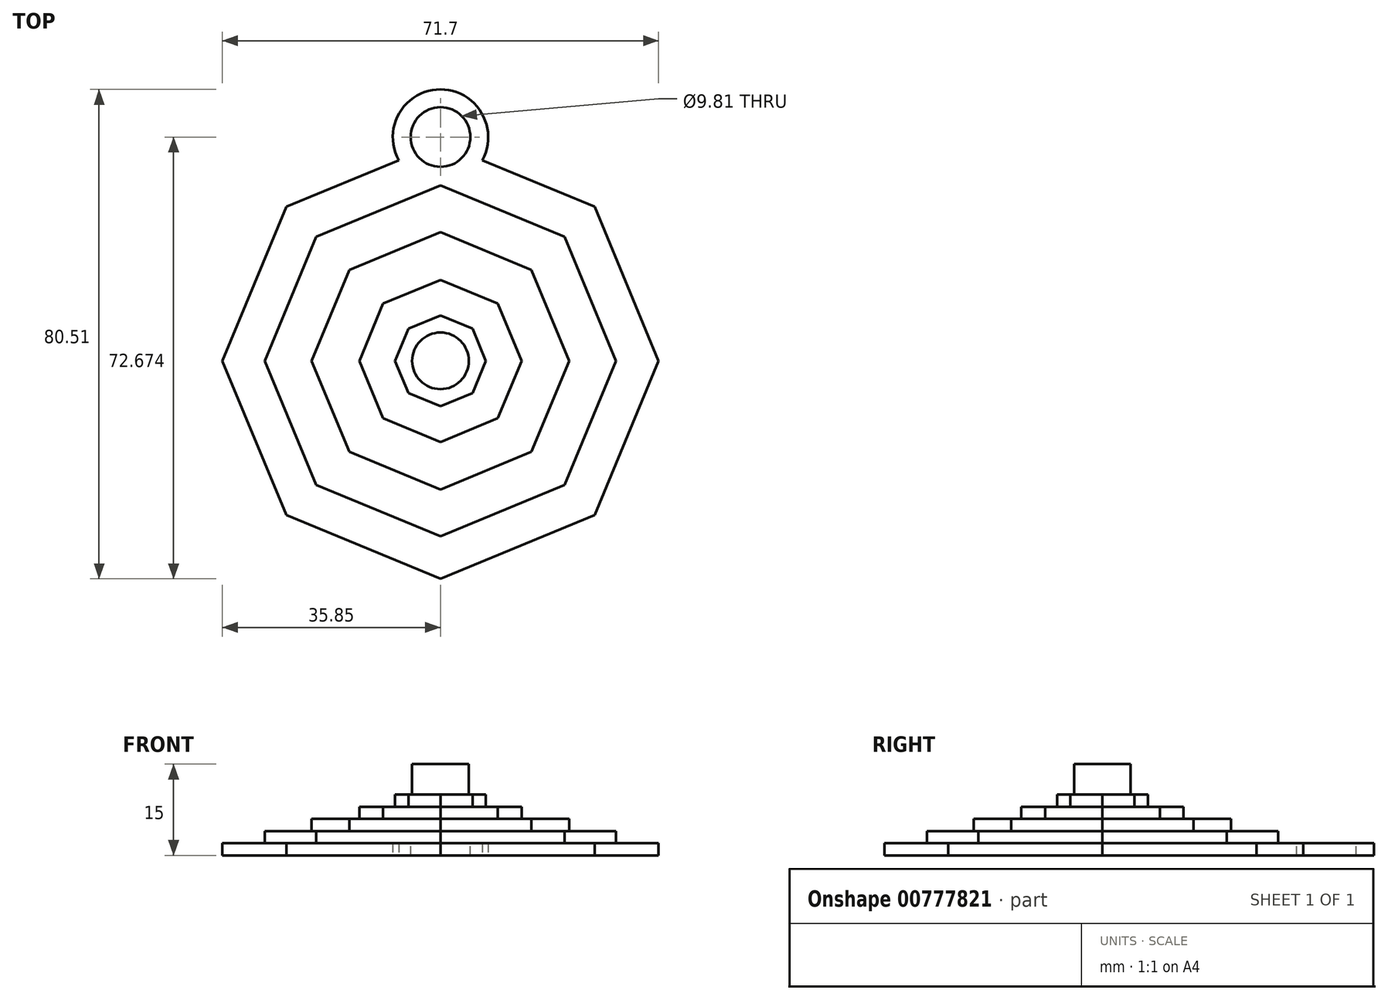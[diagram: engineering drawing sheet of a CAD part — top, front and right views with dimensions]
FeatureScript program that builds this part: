
annotation { "Feature Type Name" : "Feature", "Feature Type Description" : "" }
export const myFeature = defineFeature(function(context is Context, id is Id, definition is map)
    precondition{}
    {
        {
            var Q0;
            Q0=qCreatedBy(makeId("Top.planeOp"),FACE);
            var sketch = newSketch(context, id + "F0", { "sketchPlane" : qUnion([Q0])});
            skCircle(sketch, "E0.cCircle", {"center": v(0, 0) * mm, "radius": 35.85 * mm, "construction": true});
            skLineSegment(sketch, "E0.0", {"start": v(0, 35.85) * mm, "end": v(25.35, 25.35) * mm});
            skLineSegment(sketch, "E0.1", {"start": v(25.35, 25.35) * mm, "end": v(35.85, 0) * mm});
            skLineSegment(sketch, "E0.2", {"start": v(35.85, 0) * mm, "end": v(25.35, -25.35) * mm});
            skLineSegment(sketch, "E0.3", {"start": v(25.35, -25.35) * mm, "end": v(0, -35.85) * mm});
            skLineSegment(sketch, "E0.4", {"start": v(0, -35.85) * mm, "end": v(-25.35, -25.35) * mm});
            skLineSegment(sketch, "E0.5", {"start": v(-25.35, -25.35) * mm, "end": v(-35.85, 0) * mm});
            skLineSegment(sketch, "E0.6", {"start": v(-35.85, 0) * mm, "end": v(-25.35, 25.35) * mm});
            skLineSegment(sketch, "E0.7", {"start": v(-25.35, 25.35) * mm, "end": v(0, 35.85) * mm});
            skSolve(sketch);
        }
        {
            var Q0;
            Q0=makeQuery(id+"F0.imprint","IMPRINT",FACE,{"disambiguationData":[TD([[makeQuery(id+"F0.imprint","IMPRINT",EDGE,{"derivedFrom":sQuery(id+"F0.wireOp",EDGE,"E0.0")}),-1.0]])]});
            extrude(context, id + "F1", {"entities" : qUnion([Q0]), "depth" : 2 * mm, "offsetDistance" : 25.4 * mm});
        }
        {
            var Q0;
            Q0=makeQuery(id+"F1.opExtrude","CAP_FACE",FACE,{"disambiguationData":[OSD([sQuery(id+"F0.wireOp",EDGE,"E0.0"),sQuery(id+"F0.wireOp",EDGE,"E0.1"),sQuery(id+"F0.wireOp",EDGE,"E0.2"),sQuery(id+"F0.wireOp",EDGE,"E0.3"),sQuery(id+"F0.wireOp",EDGE,"E0.4"),sQuery(id+"F0.wireOp",EDGE,"E0.5"),sQuery(id+"F0.wireOp",EDGE,"E0.6"),sQuery(id+"F0.wireOp",EDGE,"E0.7")])],"isStart":false});
            var sketch = newSketch(context, id + "F2", { "sketchPlane" : qUnion([Q0])});
            skCircle(sketch, "E1.cCircle", {"center": v(0, 0) * mm, "radius": 28.87 * mm, "construction": true});
            skLineSegment(sketch, "E1.0", {"start": v(0, 28.87) * mm, "end": v(20.42, 20.42) * mm});
            skLineSegment(sketch, "E1.1", {"start": v(20.42, 20.42) * mm, "end": v(28.87, 0) * mm});
            skLineSegment(sketch, "E1.2", {"start": v(28.87, 0) * mm, "end": v(20.42, -20.42) * mm});
            skLineSegment(sketch, "E1.3", {"start": v(20.42, -20.42) * mm, "end": v(0, -28.87) * mm});
            skLineSegment(sketch, "E1.4", {"start": v(0, -28.87) * mm, "end": v(-20.42, -20.42) * mm});
            skLineSegment(sketch, "E1.5", {"start": v(-20.42, -20.42) * mm, "end": v(-28.87, 0) * mm});
            skLineSegment(sketch, "E1.6", {"start": v(-28.87, 0) * mm, "end": v(-20.42, 20.42) * mm});
            skLineSegment(sketch, "E1.7", {"start": v(-20.42, 20.42) * mm, "end": v(0, 28.87) * mm});
            skSolve(sketch);
        }
        {
            var Q0;
            Q0 = qSketchRegion(id + "F2", true);
            extrude(context, id + "F3", {"entities" : qUnion([Q0]), "operationType" : NewBodyOperationType.ADD, "depth" : 2 * mm, "offsetDistance" : 25.4 * mm});
        }
        {
            var Q0;
            Q0=makeQuery(id+"F3.opExtrude","CAP_FACE",FACE,{"disambiguationData":[OSD([sQuery(id+"F2.wireOp",EDGE,"E1.0"),sQuery(id+"F2.wireOp",EDGE,"E1.1"),sQuery(id+"F2.wireOp",EDGE,"E1.2"),sQuery(id+"F2.wireOp",EDGE,"E1.3"),sQuery(id+"F2.wireOp",EDGE,"E1.4"),sQuery(id+"F2.wireOp",EDGE,"E1.5"),sQuery(id+"F2.wireOp",EDGE,"E1.6"),sQuery(id+"F2.wireOp",EDGE,"E1.7")])],"isStart":false});
            var sketch = newSketch(context, id + "F4", { "sketchPlane" : qUnion([Q0])});
            skCircle(sketch, "E2.cCircle", {"center": v(0, 0) * mm, "radius": 21.16 * mm, "construction": true});
            skLineSegment(sketch, "E2.0", {"start": v(0, 21.16) * mm, "end": v(14.97, 14.97) * mm});
            skLineSegment(sketch, "E2.1", {"start": v(14.97, 14.97) * mm, "end": v(21.16, 0) * mm});
            skLineSegment(sketch, "E2.2", {"start": v(21.16, 0) * mm, "end": v(14.97, -14.97) * mm});
            skLineSegment(sketch, "E2.3", {"start": v(14.97, -14.97) * mm, "end": v(0, -21.16) * mm});
            skLineSegment(sketch, "E2.4", {"start": v(0, -21.16) * mm, "end": v(-14.97, -14.97) * mm});
            skLineSegment(sketch, "E2.5", {"start": v(-14.97, -14.97) * mm, "end": v(-21.16, 0) * mm});
            skLineSegment(sketch, "E2.6", {"start": v(-21.16, 0) * mm, "end": v(-14.97, 14.97) * mm});
            skLineSegment(sketch, "E2.7", {"start": v(-14.97, 14.97) * mm, "end": v(0, 21.16) * mm});
            skSolve(sketch);
        }
        {
            var Q0;
            Q0=makeQuery(id+"F4.imprint","IMPRINT",FACE,{"disambiguationData":[TD([[makeQuery(id+"F4.imprint","IMPRINT",EDGE,{"derivedFrom":sQuery(id+"F4.wireOp",EDGE,"E2.0")}),-1.0]])]});
            extrude(context, id + "F5", {"entities" : qUnion([Q0]), "operationType" : NewBodyOperationType.ADD, "depth" : 2 * mm, "offsetDistance" : 25.4 * mm});
        }
        {
            var Q0;
            Q0=makeQuery(id+"F5.opExtrude","CAP_FACE",FACE,{"disambiguationData":[OSD([sQuery(id+"F4.wireOp",EDGE,"E2.0"),sQuery(id+"F4.wireOp",EDGE,"E2.1"),sQuery(id+"F4.wireOp",EDGE,"E2.2"),sQuery(id+"F4.wireOp",EDGE,"E2.3"),sQuery(id+"F4.wireOp",EDGE,"E2.4"),sQuery(id+"F4.wireOp",EDGE,"E2.5"),sQuery(id+"F4.wireOp",EDGE,"E2.6"),sQuery(id+"F4.wireOp",EDGE,"E2.7")])],"isStart":false});
            var sketch = newSketch(context, id + "F6", { "sketchPlane" : qUnion([Q0])});
            skCircle(sketch, "E3.cCircle", {"center": v(0, 0) * mm, "radius": 13.34 * mm, "construction": true});
            skLineSegment(sketch, "E3.0", {"start": v(0, 13.34) * mm, "end": v(9.43, 9.43) * mm});
            skLineSegment(sketch, "E3.1", {"start": v(9.43, 9.43) * mm, "end": v(13.34, 0) * mm});
            skLineSegment(sketch, "E3.2", {"start": v(13.34, 0) * mm, "end": v(9.43, -9.43) * mm});
            skLineSegment(sketch, "E3.3", {"start": v(9.43, -9.43) * mm, "end": v(0, -13.34) * mm});
            skLineSegment(sketch, "E3.4", {"start": v(0, -13.34) * mm, "end": v(-9.43, -9.43) * mm});
            skLineSegment(sketch, "E3.5", {"start": v(-9.43, -9.43) * mm, "end": v(-13.34, 0) * mm});
            skLineSegment(sketch, "E3.6", {"start": v(-13.34, 0) * mm, "end": v(-9.43, 9.43) * mm});
            skLineSegment(sketch, "E3.7", {"start": v(-9.43, 9.43) * mm, "end": v(0, 13.34) * mm});
            skSolve(sketch);
        }
        {
            var Q0;
            Q0=makeQuery(id+"F6.imprint","IMPRINT",FACE,{"disambiguationData":[TD([[makeQuery(id+"F6.imprint","IMPRINT",EDGE,{"derivedFrom":sQuery(id+"F6.wireOp",EDGE,"E3.0")}),-1.0]])]});
            extrude(context, id + "F7", {"entities" : qUnion([Q0]), "operationType" : NewBodyOperationType.ADD, "depth" : 2 * mm, "offsetDistance" : 25.4 * mm});
        }
        {
            var Q0;
            Q0=makeQuery(id+"F7.opExtrude","CAP_FACE",FACE,{"disambiguationData":[OSD([sQuery(id+"F6.wireOp",EDGE,"E3.0"),sQuery(id+"F6.wireOp",EDGE,"E3.1"),sQuery(id+"F6.wireOp",EDGE,"E3.2"),sQuery(id+"F6.wireOp",EDGE,"E3.3"),sQuery(id+"F6.wireOp",EDGE,"E3.4"),sQuery(id+"F6.wireOp",EDGE,"E3.5"),sQuery(id+"F6.wireOp",EDGE,"E3.6"),sQuery(id+"F6.wireOp",EDGE,"E3.7")])],"isStart":false});
            var sketch = newSketch(context, id + "F8", { "sketchPlane" : qUnion([Q0])});
            skCircle(sketch, "E4.cCircle", {"center": v(0, 0) * mm, "radius": 7.46 * mm, "construction": true});
            skLineSegment(sketch, "E4.0", {"start": v(0, 7.46) * mm, "end": v(5.28, 5.28) * mm});
            skLineSegment(sketch, "E4.1", {"start": v(5.28, 5.28) * mm, "end": v(7.46, 0) * mm});
            skLineSegment(sketch, "E4.2", {"start": v(7.46, 0) * mm, "end": v(5.28, -5.28) * mm});
            skLineSegment(sketch, "E4.3", {"start": v(5.28, -5.28) * mm, "end": v(0, -7.46) * mm});
            skLineSegment(sketch, "E4.4", {"start": v(0, -7.46) * mm, "end": v(-5.28, -5.28) * mm});
            skLineSegment(sketch, "E4.5", {"start": v(-5.28, -5.28) * mm, "end": v(-7.46, 0) * mm});
            skLineSegment(sketch, "E4.6", {"start": v(-7.46, 0) * mm, "end": v(-5.28, 5.28) * mm});
            skLineSegment(sketch, "E4.7", {"start": v(-5.28, 5.28) * mm, "end": v(0, 7.46) * mm});
            skSolve(sketch);
        }
        {
            var Q0;
            Q0=makeQuery(id+"F8.imprint","IMPRINT",FACE,{"disambiguationData":[TD([[makeQuery(id+"F8.imprint","IMPRINT",EDGE,{"derivedFrom":sQuery(id+"F8.wireOp",EDGE,"E4.0")}),-1.0]])]});
            extrude(context, id + "F9", {"entities" : qUnion([Q0]), "operationType" : NewBodyOperationType.ADD, "depth" : 2 * mm, "offsetDistance" : 25.4 * mm});
        }
        {
            var Q0;
            Q0=qCreatedBy(makeId("Top.planeOp"),FACE);
            var sketch = newSketch(context, id + "F10", { "sketchPlane" : qUnion([Q0])});
            skCircle(sketch, "E5", {"center": v(0, 36.82) * mm, "radius": 7.84 * mm});
            skSolve(sketch);
        }
        {
            var Q0;
            Q0=makeQuery(id+"F10.imprint","IMPRINT",FACE,{"disambiguationData":[TD([[makeQuery(id+"F10.imprint","IMPRINT",EDGE,{"derivedFrom":sQuery(id+"F10.wireOp",EDGE,"E5")}),1.0]])]});
            extrude(context, id + "F11", {"entities" : qUnion([Q0]), "operationType" : NewBodyOperationType.ADD, "depth" : 2 * mm, "offsetDistance" : 25.4 * mm});
        }
        {
            var Q0;
            Q0=makeQuery(id+"F11.boolean.opBoolean","MERGE",FACE,{"derivedFrom":[makeQuery(id+"F1.opExtrude","CAP_FACE",FACE,{"disambiguationData":[OSD([sQuery(id+"F0.wireOp",EDGE,"E0.0"),sQuery(id+"F0.wireOp",EDGE,"E0.1"),sQuery(id+"F0.wireOp",EDGE,"E0.2"),sQuery(id+"F0.wireOp",EDGE,"E0.3"),sQuery(id+"F0.wireOp",EDGE,"E0.4"),sQuery(id+"F0.wireOp",EDGE,"E0.5"),sQuery(id+"F0.wireOp",EDGE,"E0.6"),sQuery(id+"F0.wireOp",EDGE,"E0.7")])],"isStart":false}),makeQuery(id+"F11.opExtrude","CAP_FACE",FACE,{"disambiguationData":[OSD([sQuery(id+"F10.wireOp",EDGE,"E5")])],"isStart":false})]});
            var sketch = newSketch(context, id + "F12", { "sketchPlane" : qUnion([Q0])});
            skCircle(sketch, "E6", {"center": v(0, 36.82) * mm, "radius": 4.9 * mm});
            skSolve(sketch);
        }
        {
            var Q0;
            Q0=makeQuery(id+"F12.imprint","IMPRINT",FACE,{"disambiguationData":[TD([[makeQuery(id+"F12.imprint","IMPRINT",EDGE,{"derivedFrom":sQuery(id+"F12.wireOp",EDGE,"E6")}),1.0]])]});
            extrude(context, id + "F13", {"entities" : qUnion([Q0]), "operationType" : NewBodyOperationType.REMOVE, "oppositeDirection" : true, "depth" : 25.4 * mm, "offsetDistance" : 25.4 * mm});
        }
        {
            var Q0;
            Q0=makeQuery(id+"F9.opExtrude","CAP_FACE",FACE,{"disambiguationData":[OSD([sQuery(id+"F8.wireOp",EDGE,"E4.0"),sQuery(id+"F8.wireOp",EDGE,"E4.1"),sQuery(id+"F8.wireOp",EDGE,"E4.2"),sQuery(id+"F8.wireOp",EDGE,"E4.3"),sQuery(id+"F8.wireOp",EDGE,"E4.4"),sQuery(id+"F8.wireOp",EDGE,"E4.5"),sQuery(id+"F8.wireOp",EDGE,"E4.6"),sQuery(id+"F8.wireOp",EDGE,"E4.7")])],"isStart":false});
            var sketch = newSketch(context, id + "F14", { "sketchPlane" : qUnion([Q0])});
            skCircle(sketch, "E7", {"center": v(0, 0) * mm, "radius": 4.66 * mm});
            skSolve(sketch);
        }
        {
            var Q0;
            Q0=makeQuery(id+"F14.imprint","IMPRINT",FACE,{"disambiguationData":[TD([[makeQuery(id+"F14.imprint","IMPRINT",EDGE,{"derivedFrom":sQuery(id+"F14.wireOp",EDGE,"E7")}),1.0]])]});
            extrude(context, id + "F15", {"entities" : qUnion([Q0]), "operationType" : NewBodyOperationType.ADD, "depth" : 5 * mm, "offsetDistance" : 25.4 * mm});
        }
    });
